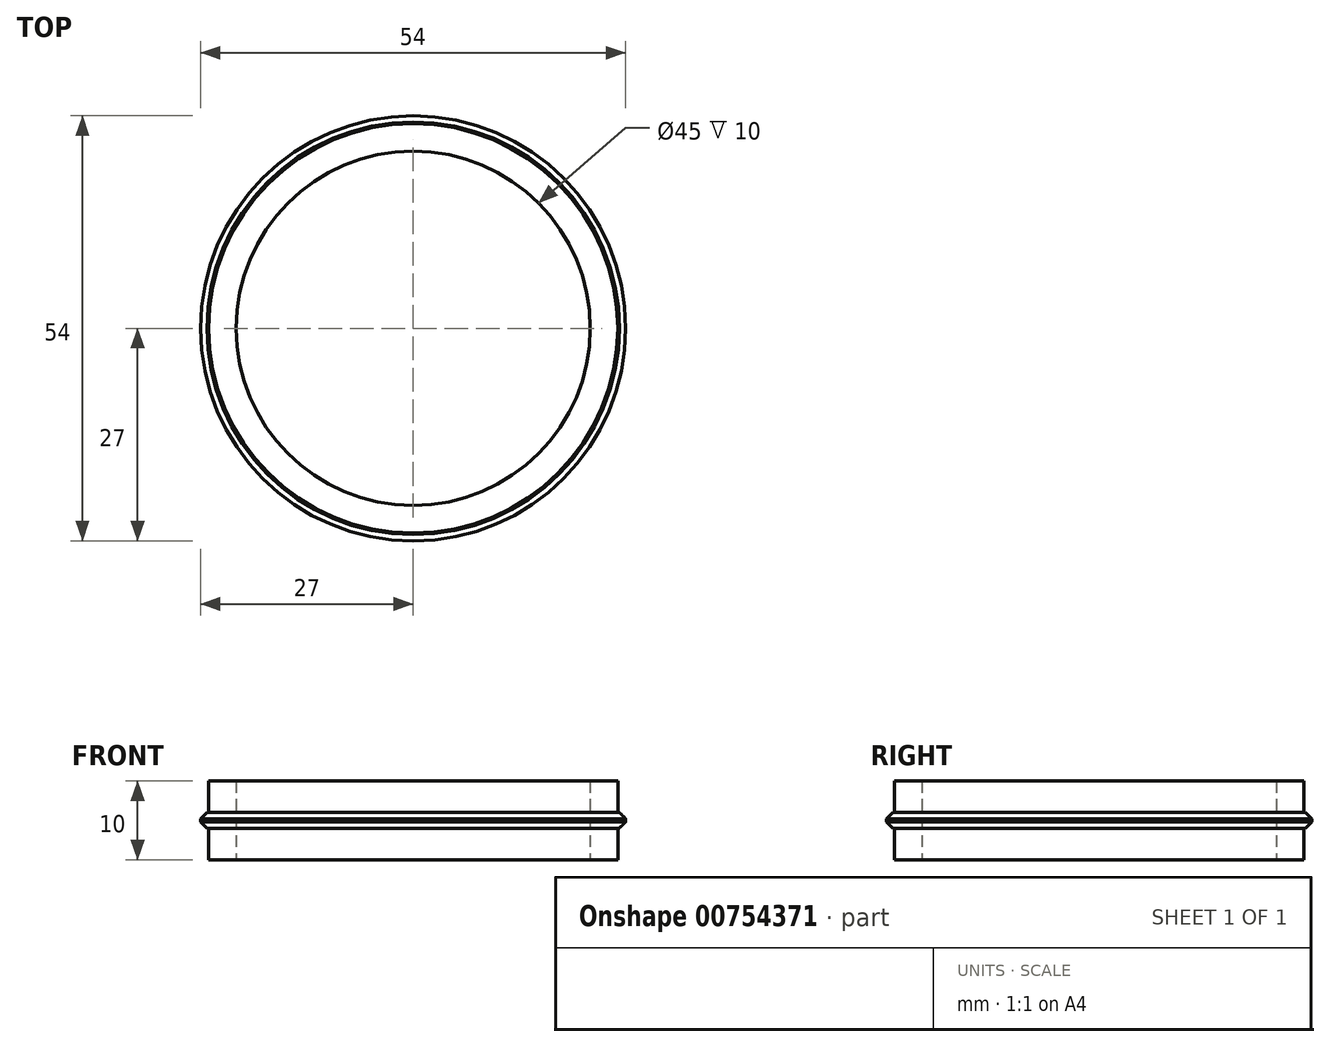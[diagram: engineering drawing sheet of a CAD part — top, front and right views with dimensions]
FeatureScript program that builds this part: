
annotation { "Feature Type Name" : "Feature", "Feature Type Description" : "" }
export const myFeature = defineFeature(function(context is Context, id is Id, definition is map)
    precondition{}
    {
        {
            var Q0;
            Q0=qCreatedBy(makeId("Top.planeOp"),FACE);
            var sketch = newSketch(context, id + "F0", { "sketchPlane" : qUnion([Q0])});
            skCircle(sketch, "E0", {"center": v(0, 0) * mm, "radius": 27 * mm});
            skCircle(sketch, "E1", {"center": v(0, 0) * mm, "radius": 26 * mm});
            skCircle(sketch, "E2", {"center": v(0, 0) * mm, "radius": 22.5 * mm});
            skSolve(sketch);
        }
        {
            var Q0;
            Q0=makeQuery(id+"F0.imprint","IMPRINT",FACE,{"disambiguationData":[TD([[makeQuery(id+"F0.imprint","IMPRINT",EDGE,{"derivedFrom":sQuery(id+"F0.wireOp",EDGE,"E0")}),1.0]])]});
            extrude(context, id + "F1", {"entities" : qUnion([Q0]), "depth" : 2 * mm, "offsetDistance" : 25 * mm, "symmetric" : true});
        }
        {
            var Q0;
            Q0=makeQuery(id+"F0.imprint","IMPRINT",FACE,{"disambiguationData":[TD([[makeQuery(id+"F0.imprint","IMPRINT",EDGE,{"derivedFrom":sQuery(id+"F0.wireOp",EDGE,"E1")}),1.0]])]});
            extrude(context, id + "F2", {"entities" : qUnion([Q0]), "operationType" : NewBodyOperationType.ADD, "depth" : 10 * mm, "offsetDistance" : 25 * mm, "symmetric" : true});
        }
        {
            var Q0;
            Q0=makeQuery(id+"F1.opExtrude","CAP_EDGE",EDGE,{"disambiguationData":[OSD([sQuery(id+"F0.wireOp",EDGE,"E0")])],"isStart":false});
            var Q1;
            Q1=makeQuery(id+"F1.opExtrude","CAP_EDGE",EDGE,{"disambiguationData":[OSD([sQuery(id+"F0.wireOp",EDGE,"E0")])],"isStart":true});
            chamfer(context, id + "F3", {"entities" : qUnion([Q0, Q1]), "width" : 0.8 * mm, "tangentPropagation" : true});
        }
    });
